# Revit family: LAMP_PUZZLE TR FRAME CORNER
name_source: partatom
category: Modelos genéricos
revit_build: Autodesk Revit 2015 (Build: 20140606_1530(x64)
units: mm (PartAtom-declared; Revit-internal decimal feet)

## types (4) — shared parameters
Accessory Type = Assembly
Comentarios de tipo = Availability of changing between standard frame Types when placed in a project.
Elevación por defecto = 1219 mm
Fabricante = LAMP
Installation instructions = http://www.lamp.es
Last update = 25/07/2018
Manufacturer URL = http://www.lamp.es
Manufacturer country = Spain
Manufacturer name = LAMP
Model explanation = Availability of changing between standard frame Types when placed in a project.
Product datasheet = http://www.lamp.es
Weight = 0.25 kg

## per-type parameters (varying)
| type | Descripción | Dimensions | Distancia | Finish | Material marco | Modelo | Product code | Recessed dimensions |
| Exterior L BLACK | PUZZLE ACC. HIDDEN FRAME 90º CORNER BK. | 270 x 270 | 271 mm | Shiny black | LAMP_Aluminio frame Puzzle BL | PUTRFRCRB | PUTRFRCRB | 258 x 258 |
| Exterior L WHITE | PUZZLE ACC. HIDDEN FRAME 90º CORNER WH. | 270 x 270 | 271 mm | Shiny white | LAMP_Aluminio frame Puzzle WH | PUTRFRCRW | PUTRFRCRW | 258 x 258 |
| Interior L BLACK | PUZZLE ACC. HIDDEN FRAME 90º CORNER BK. | 92,4 x 92,4 | 92 mm | Shiny black | LAMP_Aluminio frame Puzzle BL | PUTRFRCRB | PUTRFRCRB | 80,4 x 80,4 |
| Interior L WHITE | PUZZLE ACC. HIDDEN FRAME 90º CORNER WH. | 92,4 x 92,4 | 92 mm | Shiny white | LAMP_Aluminio frame Puzzle WH | PUTRFRCRW | PUTRFRCRW | 80,4 x 80,4 |
